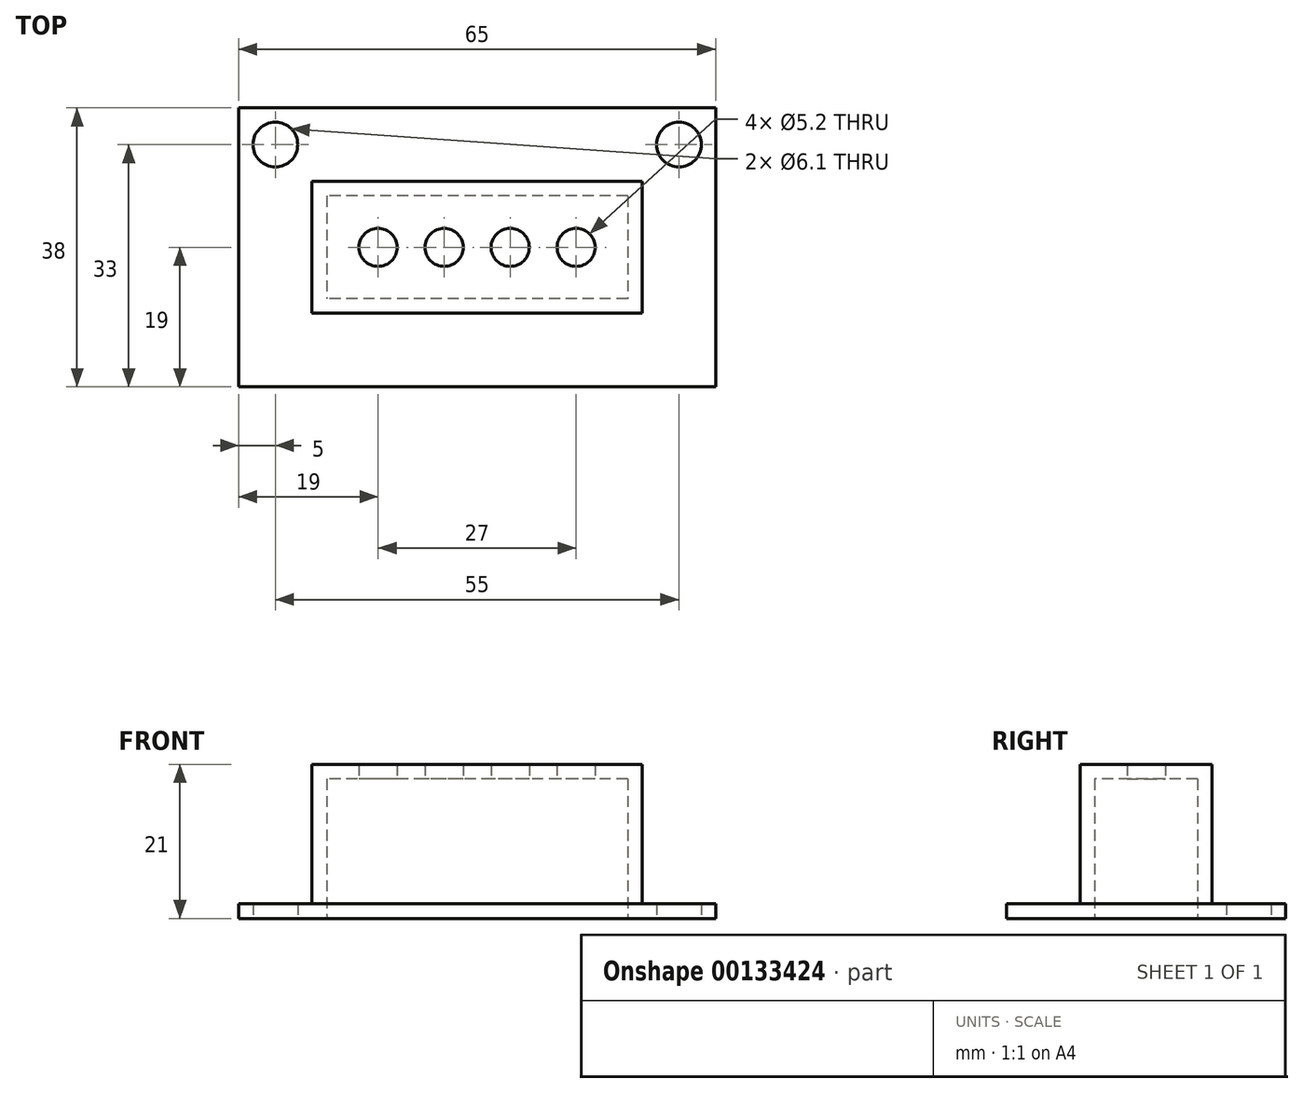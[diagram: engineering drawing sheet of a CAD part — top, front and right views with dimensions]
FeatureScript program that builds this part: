
annotation { "Feature Type Name" : "Feature", "Feature Type Description" : "" }
export const myFeature = defineFeature(function(context is Context, id is Id, definition is map)
    precondition{}
    {
        {
            var Q0;
            Q0=qCreatedBy(makeId("Top.planeOp"),FACE);
            var sketch = newSketch(context, id + "F0", { "sketchPlane" : qUnion([Q0])});
            skLineSegment(sketch, "E0.bottom", {"start": v(22.5, 9) * mm, "end": v(-22.5, 9) * mm});
            skLineSegment(sketch, "E0.top", {"start": v(22.5, -9) * mm, "end": v(-22.5, -9) * mm});
            skLineSegment(sketch, "E0.left", {"start": v(22.5, 9) * mm, "end": v(22.5, -9) * mm});
            skLineSegment(sketch, "E0.right", {"start": v(-22.5, 9) * mm, "end": v(-22.5, -9) * mm});
            skPoint(sketch, "E0.middle", {"position": v(0, 0) * mm});
            skLineSegment(sketch, "E1", {"start": v(-22.5, -9) * mm, "end": v(-22.5, 0) * mm});
            skLineSegment(sketch, "E2", {"start": v(-22.5, 0) * mm, "end": v(22.5, 0) * mm});
            skLineSegment(sketch, "E3", {"start": v(-13.5, 0) * mm, "end": v(-4.5, 0) * mm, "construction": true});
            skCircle(sketch, "E4", {"center": v(-4.5, 0) * mm, "radius": 2.6 * mm});
            skCircle(sketch, "E5.MirrorC", {"center": v(4.5, 0) * mm, "radius": 2.6 * mm});
            skLineSegment(sketch, "E6.0", {"start": v(20.5, -7) * mm, "end": v(-20.5, -7) * mm});
            skLineSegment(sketch, "E6.1", {"start": v(20.5, 7) * mm, "end": v(20.5, -7) * mm});
            skLineSegment(sketch, "E6.2", {"start": v(20.5, 7) * mm, "end": v(-20.5, 7) * mm});
            skLineSegment(sketch, "E6.3", {"start": v(-20.5, 7) * mm, "end": v(-20.5, -7) * mm});
            skCircle(sketch, "E7", {"center": v(-13.5, 0) * mm, "radius": 2.6 * mm});
            skLineSegment(sketch, "E8", {"start": v(4.5, 0) * mm, "end": v(4.5, 0) * mm});
            skCircle(sketch, "E9.MirrorC", {"center": v(13.5, 0) * mm, "radius": 2.6 * mm});
            skLineSegment(sketch, "E10.0", {"start": v(32.5, 19) * mm, "end": v(-32.5, 19) * mm});
            skLineSegment(sketch, "E10.1", {"start": v(32.5, 19) * mm, "end": v(32.5, -19) * mm});
            skLineSegment(sketch, "E10.2", {"start": v(32.5, -19) * mm, "end": v(-32.5, -19) * mm});
            skLineSegment(sketch, "E10.3", {"start": v(-32.5, 19) * mm, "end": v(-32.5, -19) * mm});
            skLineSegment(sketch, "E11", {"start": v(-32.5, 19) * mm, "end": v(-32.5, 14) * mm});
            skLineSegment(sketch, "E12", {"start": v(-32.5, 14) * mm, "end": v(-27.5, 14) * mm});
            skLineSegment(sketch, "E13", {"start": v(-13.5, 0) * mm, "end": v(-27.5, 0) * mm});
            skLineSegment(sketch, "E14", {"start": v(-27.5, 0) * mm, "end": v(-27.5, 14) * mm});
            skCircle(sketch, "E15.MirrorC", {"center": v(27.5, 14) * mm, "radius": 3.05 * mm});
            skCircle(sketch, "E16.MirrorC", {"center": v(-27.5, 14) * mm, "radius": 3.05 * mm});
            skSolve(sketch);
        }
        {
            var Q0;
            {var subQ8=sQuery(id+"F0.wireOp",EDGE,"E0.top");Q0=makeQuery(id+"F0.imprint","IMPRINT",FACE,{"disambiguationData":[TD([[makeQuery(id+"F0.imprint","IMPRINT",EDGE,{"derivedFrom":subQ8}),-1.0]])]});}
            var Q1;
            {var subQ6=sQuery(id+"F0.wireOp",EDGE,"E0.bottom");Q1=makeQuery(id+"F0.imprint","IMPRINT",FACE,{"disambiguationData":[TD([[makeQuery(id+"F0.imprint","IMPRINT",EDGE,{"derivedFrom":subQ6}),1.0]])]});}
            extrude(context, id + "F1", {"entities" : qUnion([Q0, Q1]), "depth" : 21 * mm});
        }
        {
            var Q0;
            {var subQ8=sQuery(id+"F0.wireOp",EDGE,"E6.2");Q0=makeQuery(id+"F0.imprint","IMPRINT",FACE,{"disambiguationData":[TD([[makeQuery(id+"F0.imprint","IMPRINT",EDGE,{"derivedFrom":subQ8}),1.0]])]});}
            var Q1;
            {var subQ0=sQuery(id+"F0.wireOp",EDGE,"E6.0");Q1=makeQuery(id+"F0.imprint","IMPRINT",FACE,{"disambiguationData":[TD([[makeQuery(id+"F0.imprint","IMPRINT",EDGE,{"derivedFrom":subQ0}),-1.0]])]});}
            extrude(context, id + "F2", {"entities" : qUnion([Q0, Q1]), "operationType" : NewBodyOperationType.ADD, "depth" : 21 * mm, "hasSecondDirection" : true, "secondDirectionOppositeDirection" : false, "secondDirectionDepth" : 19 * mm});
        }
        {
            var Q0;
            {var subQ0=sQuery(id+"F0.wireOp",EDGE,"E0.bottom");Q0=makeQuery(id+"F0.imprint","IMPRINT",FACE,{"disambiguationData":[TD([[makeQuery(id+"F0.imprint","IMPRINT",EDGE,{"derivedFrom":subQ0}),-1.0]])]});}
            extrude(context, id + "F3", {"entities" : qUnion([Q0]), "operationType" : NewBodyOperationType.ADD, "depth" : 2 * mm});
        }
    });
